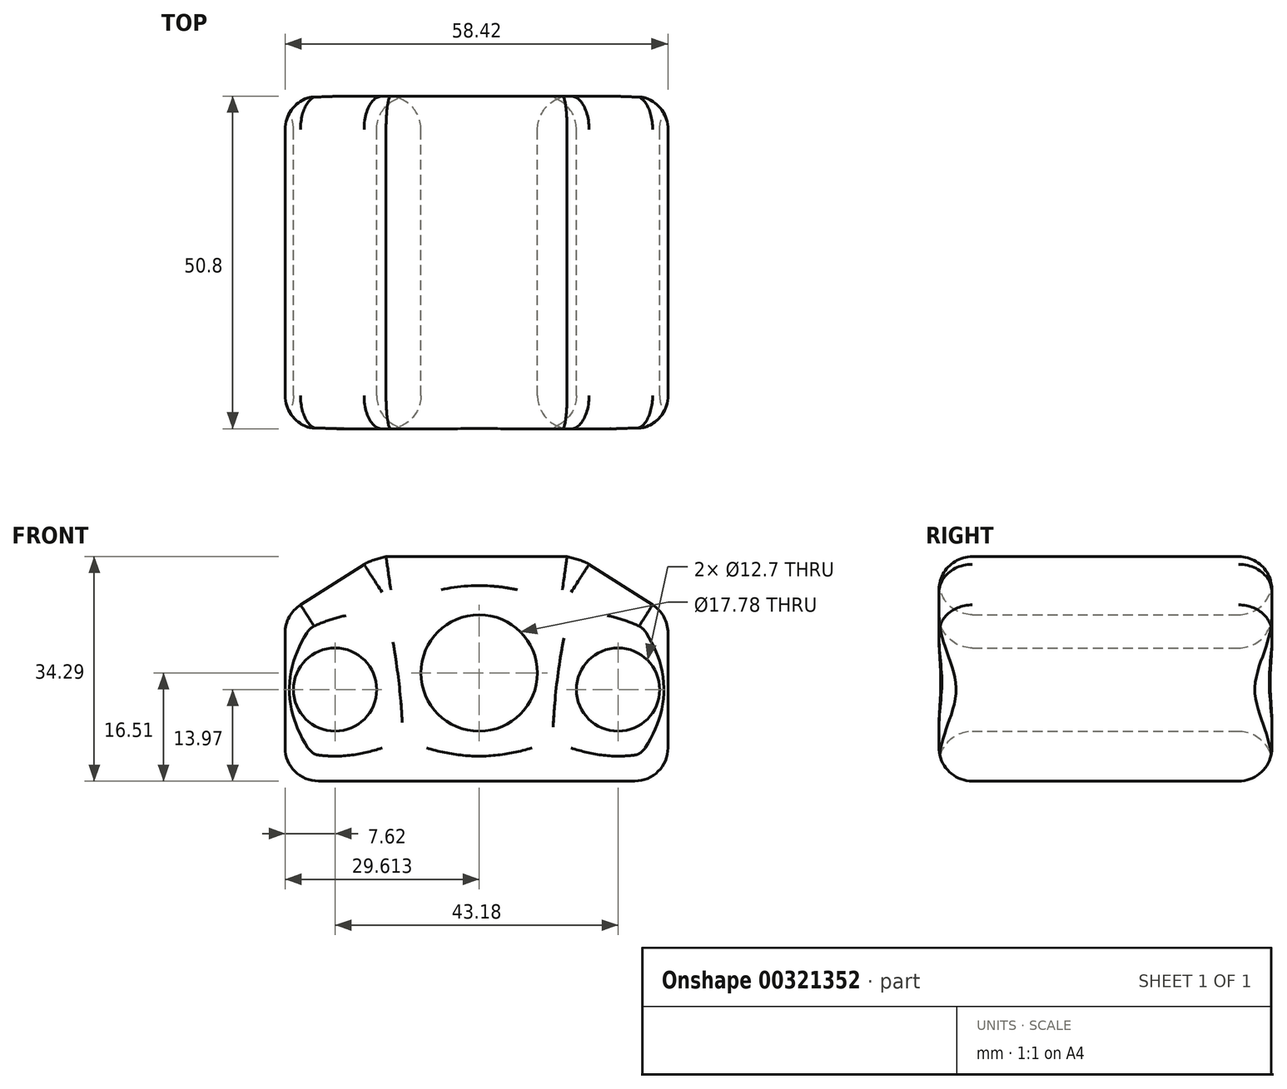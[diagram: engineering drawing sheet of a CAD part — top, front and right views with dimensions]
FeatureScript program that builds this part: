
annotation { "Feature Type Name" : "Feature", "Feature Type Description" : "" }
export const myFeature = defineFeature(function(context is Context, id is Id, definition is map)
    precondition{}
    {
        {
            var Q0;
            Q0=qCreatedBy(makeId("Front.planeOp"),FACE);
            var sketch = newSketch(context, id + "F0", { "sketchPlane" : qUnion([Q0])});
            skLineSegment(sketch, "E0", {"start": v(0, 0) * mm, "end": v(0, 25.4) * mm});
            skLineSegment(sketch, "E1", {"start": v(0, 25.4) * mm, "end": v(13.91, 34.29) * mm});
            skLineSegment(sketch, "E2", {"start": v(13.91, 34.3) * mm, "end": v(44.5, 34.3) * mm});
            skLineSegment(sketch, "E3", {"start": v(44.5, 34.3) * mm, "end": v(58.42, 25.4) * mm});
            skLineSegment(sketch, "E4", {"start": v(58.42, 25.4) * mm, "end": v(58.42, 0) * mm});
            skLineSegment(sketch, "E5", {"start": v(58.42, 0) * mm, "end": v(0, 0) * mm});
            skCircle(sketch, "E6", {"center": v(7.62, 13.97) * mm, "radius": 6.35 * mm});
            skCircle(sketch, "E7", {"center": v(29.61, 16.5) * mm, "radius": 8.9 * mm});
            skCircle(sketch, "E8", {"center": v(50.8, 13.97) * mm, "radius": 6.35 * mm});
            skSolve(sketch);
        }
        {
            var Q0;
            Q0 = qSketchRegion(id + "F0", true);
            extrude(context, id + "F1", {"entities" : qUnion([Q0]), "depth" : 50.8 * mm});
        }
        {
            var Q0;
            Q0=makeQuery(id+"F1.opExtrude","CAP_FACE",FACE,{"disambiguationData":[OSD([sQuery(id+"F0.wireOp",EDGE,"E0"),sQuery(id+"F0.wireOp",EDGE,"E1"),sQuery(id+"F0.wireOp",EDGE,"E2"),sQuery(id+"F0.wireOp",EDGE,"E3"),sQuery(id+"F0.wireOp",EDGE,"E4"),sQuery(id+"F0.wireOp",EDGE,"E5"),sQuery(id+"F0.wireOp",EDGE,"E6"),sQuery(id+"F0.wireOp",EDGE,"E7"),sQuery(id+"F0.wireOp",EDGE,"E8")])],"isStart":false});
            fillet(context, id + "F2", {"entities" : qUnion([Q0]), "radius" : 5.08 * mm, "tangentPropagation" : true, "allowEdgeOverflow" : false});
        }
        {
            var Q0;
            Q0=makeQuery(id+"F1.opExtrude","CAP_FACE",FACE,{"disambiguationData":[OSD([sQuery(id+"F0.wireOp",EDGE,"E0"),sQuery(id+"F0.wireOp",EDGE,"E1"),sQuery(id+"F0.wireOp",EDGE,"E2"),sQuery(id+"F0.wireOp",EDGE,"E3"),sQuery(id+"F0.wireOp",EDGE,"E4"),sQuery(id+"F0.wireOp",EDGE,"E5"),sQuery(id+"F0.wireOp",EDGE,"E6"),sQuery(id+"F0.wireOp",EDGE,"E7"),sQuery(id+"F0.wireOp",EDGE,"E8")])],"isStart":true});
            fillet(context, id + "F3", {"entities" : qUnion([Q0]), "radius" : 5.08 * mm, "tangentPropagation" : true, "allowEdgeOverflow" : false});
        }
        {
            var Q0;
            Q0=makeQuery(id+"F1.opExtrude","SWEPT_FACE",FACE,{"disambiguationData":[OSD([sQuery(id+"F0.wireOp",EDGE,"E2")])]});
            chamfer(context, id + "F4", {"entities" : qUnion([Q0]), "width" : 5.08 * mm, "tangentPropagation" : true});
        }
        {
            var Q0;
            Q0=makeQuery(id+"F1.opExtrude","SWEPT_FACE",FACE,{"disambiguationData":[OSD([sQuery(id+"F0.wireOp",EDGE,"E1")])]});
            fillet(context, id + "F5", {"entities" : qUnion([Q0]), "radius" : 5.08 * mm, "tangentPropagation" : true, "allowEdgeOverflow" : false});
        }
        {
            var Q0;
            Q0=makeQuery(id+"F1.opExtrude","SWEPT_FACE",FACE,{"disambiguationData":[OSD([sQuery(id+"F0.wireOp",EDGE,"E3")])]});
            fillet(context, id + "F6", {"entities" : qUnion([Q0]), "radius" : 5.08 * mm, "tangentPropagation" : true, "allowEdgeOverflow" : false});
        }
        {
            var Q0;
            Q0=makeQuery(id+"F1.opExtrude","SWEPT_FACE",FACE,{"disambiguationData":[OSD([sQuery(id+"F0.wireOp",EDGE,"E5")])]});
            fillet(context, id + "F7", {"entities" : qUnion([Q0]), "radius" : 5.08 * mm, "tangentPropagation" : true, "allowEdgeOverflow" : false});
        }
    });
